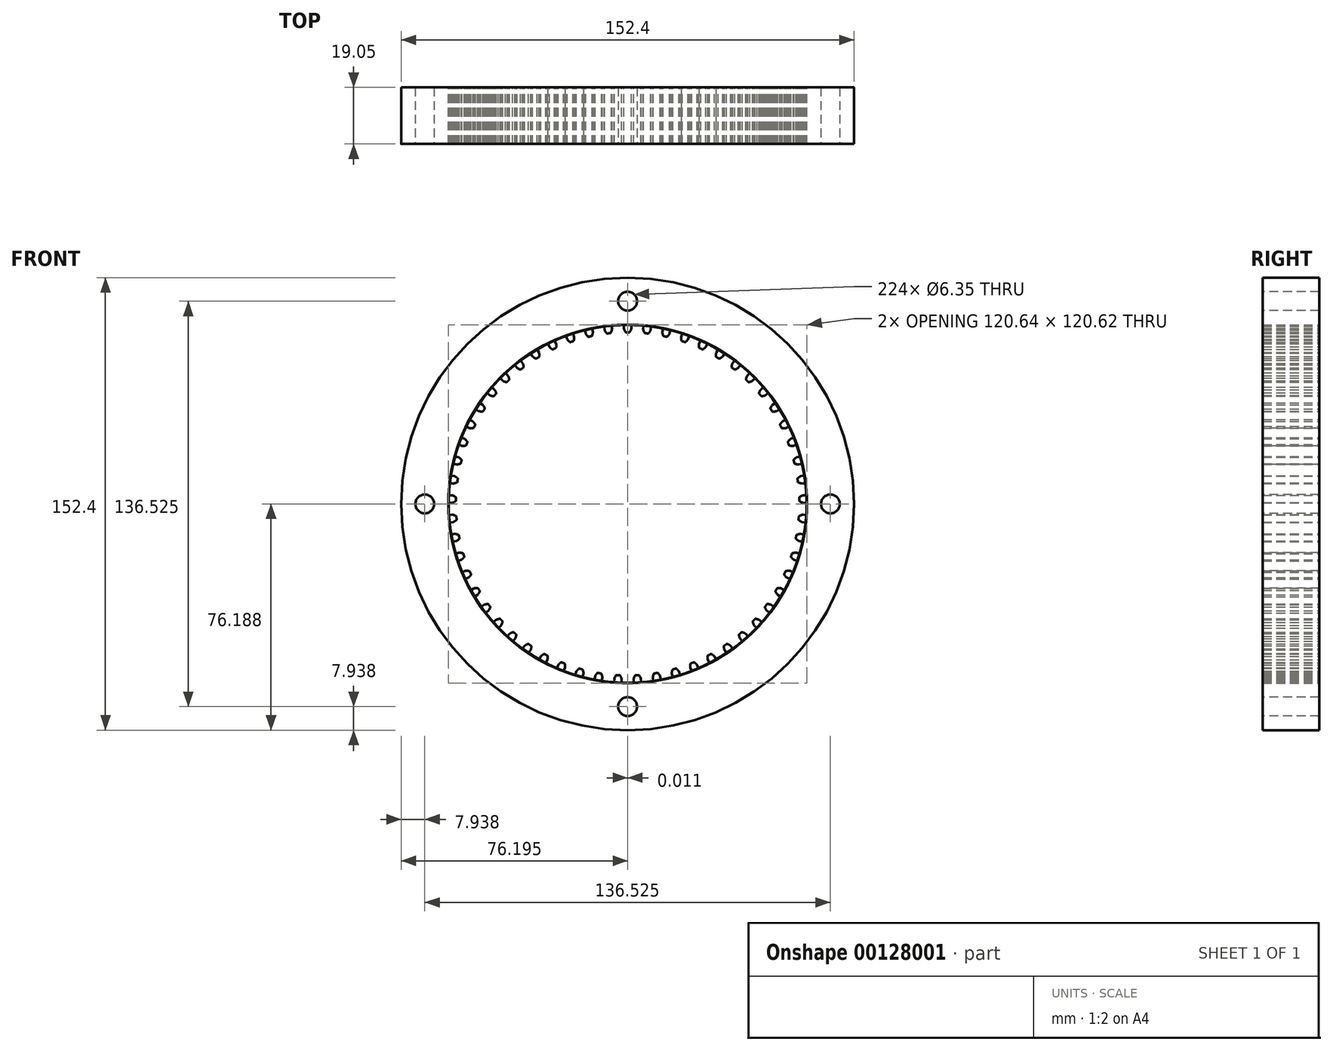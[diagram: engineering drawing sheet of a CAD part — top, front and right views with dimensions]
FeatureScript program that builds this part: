
annotation { "Feature Type Name" : "Feature", "Feature Type Description" : "" }
export const myFeature = defineFeature(function(context is Context, id is Id, definition is map)
    precondition{}
    {
        {
            var Q0;
            Q0=qCreatedBy(makeId("Front.planeOp"),FACE);
            var sketch = newSketch(context, id + "F0", { "sketchPlane" : qUnion([Q0])});
            skCircle(sketch, "E0", {"center": v(0, 0) * mm, "radius": 59.06 * mm, "construction": true});
            skCircle(sketch, "E1", {"center": v(0, 0) * mm, "radius": 60.33 * mm});
            skArc(sketch, "E2", {"start": v(0, 60.33) * mm, "mid": v(0.62, 60.32) * mm, "end": v(1.25, 60.31) * mm});
            skLineSegment(sketch, "E3", {"start": v(1.25, 60.31) * mm, "end": v(1.25, 59.04) * mm});
            skCircle(sketch, "E4", {"center": v(0, 0) * mm, "radius": 57.79 * mm, "construction": true});
            skArc(sketch, "E5", {"start": v(0, 57.79) * mm, "mid": v(0.25, 57.78) * mm, "end": v(0.5, 57.78) * mm});
            skFitSpline(sketch, "E6", {"points": [v(0.63, 57.78) * mm, v(1.25, 59.04) * mm, v(1.25, 60.31) * mm], "startDerivative": vector(1.5, 2.42) * mm, "endDerivative": vector(-0.3, 2.64) * mm});
            skArc(sketch, "E7.filletArc", {"start": v(0.5, 57.78) * mm, "mid": v(0.62, 57.81) * mm, "end": v(0.71, 57.9) * mm});
            skArc(sketch, "E8.MirrorCS", {"start": v(0, 57.79) * mm, "mid": v(-0.25, 57.78) * mm, "end": v(-0.5, 57.78) * mm});
            skArc(sketch, "E9.MirrorCS", {"start": v(-0.5, 57.78) * mm, "mid": v(-0.62, 57.81) * mm, "end": v(-0.71, 57.9) * mm});
            skFitSpline(sketch, "E10.MirrorCS", {"points": [v(-0.63, 57.78) * mm, v(-1.25, 59.04) * mm, v(-1.25, 60.31) * mm], "startDerivative": vector(-1.5, 2.42) * mm, "endDerivative": vector(0.3, 2.64) * mm});
            skLineSegment(sketch, "E11.MirrorCS", {"start": v(-1.25, 60.31) * mm, "end": v(-1.25, 59.04) * mm});
            skCircle(sketch, "E12", {"center": v(0, 0) * mm, "radius": 76.2 * mm});
            skSolve(sketch);
        }
        {
            var Q0;
            Q0=makeQuery(id+"F0.imprint","IMPRINT",FACE,{"disambiguationData":[TD([[makeQuery(id+"F0.imprint","IMPRINT",EDGE,{"derivedFrom":sQuery(id+"F0.wireOp",EDGE,"E12")}),1.0]])]});
            var Q1;
            {var subQ0=sQuery(id+"F0.wireOp",EDGE,"E3");Q1=makeQuery(id+"F0.imprint","IMPRINT",FACE,{"disambiguationData":[TD([[makeQuery(id+"F0.imprint","IMPRINT",EDGE,{"derivedFrom":subQ0}),-1.0]])]});}
            extrude(context, id + "F1", {"entities" : qUnion([Q0, Q1]), "depth" : 19.05 * mm});
        }
        {
            var Q0;
            Q0=makeQuery(id+"F1.opExtrude","SWEPT_BODY",BODY,{"disambiguationData":[OSD([sQuery(id+"F0.wireOp",EDGE,"E1"),sQuery(id+"F0.wireOp",EDGE,"E3"),sQuery(id+"F0.wireOp",EDGE,"E5"),sQuery(id+"F0.wireOp",EDGE,"E6"),sQuery(id+"F0.wireOp",EDGE,"E7.filletArc"),sQuery(id+"F0.wireOp",EDGE,"E8.MirrorCS"),sQuery(id+"F0.wireOp",EDGE,"E9.MirrorCS"),sQuery(id+"F0.wireOp",EDGE,"E10.MirrorCS"),sQuery(id+"F0.wireOp",EDGE,"E11.MirrorCS"),sQuery(id+"F0.wireOp",EDGE,"E12")])]});
            var Q1;
            Q1=makeQuery(id+"F1.opExtrude","SWEPT_FACE",FACE,{"disambiguationData":[OSD([sQuery(id+"F0.wireOp",EDGE,"E1")])]});
            circularPattern(context, id + "F2", {"entities" : qUnion([Q0]), "axis" : qUnion([Q1]), "angle" : 6.32 * degree, "instanceCount" : 57});
        }
        {
            var Q0;
            Q0=makeQuery(id+"F2.opPattern","COPY",FACE,{"derivedFrom":makeQuery(id+"F1.opExtrude","CAP_FACE",FACE,{"disambiguationData":[OSD([sQuery(id+"F0.wireOp",EDGE,"E1"),sQuery(id+"F0.wireOp",EDGE,"E3"),sQuery(id+"F0.wireOp",EDGE,"E5"),sQuery(id+"F0.wireOp",EDGE,"E6"),sQuery(id+"F0.wireOp",EDGE,"E7.filletArc"),sQuery(id+"F0.wireOp",EDGE,"E8.MirrorCS"),sQuery(id+"F0.wireOp",EDGE,"E9.MirrorCS"),sQuery(id+"F0.wireOp",EDGE,"E10.MirrorCS"),sQuery(id+"F0.wireOp",EDGE,"E11.MirrorCS"),sQuery(id+"F0.wireOp",EDGE,"E12")])],"isStart":false}),"instanceName":"27"});
            var sketch = newSketch(context, id + "F3", { "sketchPlane" : qUnion([Q0])});
            skCircle(sketch, "E13", {"center": v(0, 68.26) * mm, "radius": 3.18 * mm});
            skCircle(sketch, "E14.1.0", {"center": v(-68.26, 0) * mm, "radius": 3.18 * mm});
            skCircle(sketch, "E14.2.0", {"center": v(0, -68.26) * mm, "radius": 3.18 * mm});
            skCircle(sketch, "E14.3.0", {"center": v(68.26, 0) * mm, "radius": 3.18 * mm});
            skPoint(sketch, "E14.center", {"position": v(0, 0) * mm});
            skSolve(sketch);
        }
        {
            var Q0;
            Q0=sQuery(id+"F3.wireOp",VERTEX,"E13.center");
            var Q1;
            Q1=sQuery(id+"F3.wireOp",VERTEX,"E14.3.0.center");
            var Q2;
            Q2=sQuery(id+"F3.wireOp",VERTEX,"E14.2.0.center");
            var Q3;
            Q3=sQuery(id+"F3.wireOp",VERTEX,"E14.1.0.center");
            var Q4;
            Q4=makeQuery(id+"F1.opExtrude","SWEPT_BODY",BODY,{"disambiguationData":[OSD([sQuery(id+"F0.wireOp",EDGE,"E1"),sQuery(id+"F0.wireOp",EDGE,"E3"),sQuery(id+"F0.wireOp",EDGE,"E5"),sQuery(id+"F0.wireOp",EDGE,"E6"),sQuery(id+"F0.wireOp",EDGE,"E7.filletArc"),sQuery(id+"F0.wireOp",EDGE,"E8.MirrorCS"),sQuery(id+"F0.wireOp",EDGE,"E9.MirrorCS"),sQuery(id+"F0.wireOp",EDGE,"E10.MirrorCS"),sQuery(id+"F0.wireOp",EDGE,"E11.MirrorCS"),sQuery(id+"F0.wireOp",EDGE,"E12")])]});
            var Q5;
            Q5=makeQuery(id+"F2.opPattern","COPY",BODY,{"derivedFrom":makeQuery(id+"F1.opExtrude","SWEPT_BODY",BODY,{"disambiguationData":[OSD([sQuery(id+"F0.wireOp",EDGE,"E1"),sQuery(id+"F0.wireOp",EDGE,"E3"),sQuery(id+"F0.wireOp",EDGE,"E5"),sQuery(id+"F0.wireOp",EDGE,"E6"),sQuery(id+"F0.wireOp",EDGE,"E7.filletArc"),sQuery(id+"F0.wireOp",EDGE,"E8.MirrorCS"),sQuery(id+"F0.wireOp",EDGE,"E9.MirrorCS"),sQuery(id+"F0.wireOp",EDGE,"E10.MirrorCS"),sQuery(id+"F0.wireOp",EDGE,"E11.MirrorCS"),sQuery(id+"F0.wireOp",EDGE,"E12")])]}),"instanceName":"1"});
            var Q6;
            Q6=makeQuery(id+"F2.opPattern","COPY",BODY,{"derivedFrom":makeQuery(id+"F1.opExtrude","SWEPT_BODY",BODY,{"disambiguationData":[OSD([sQuery(id+"F0.wireOp",EDGE,"E1"),sQuery(id+"F0.wireOp",EDGE,"E3"),sQuery(id+"F0.wireOp",EDGE,"E5"),sQuery(id+"F0.wireOp",EDGE,"E6"),sQuery(id+"F0.wireOp",EDGE,"E7.filletArc"),sQuery(id+"F0.wireOp",EDGE,"E8.MirrorCS"),sQuery(id+"F0.wireOp",EDGE,"E9.MirrorCS"),sQuery(id+"F0.wireOp",EDGE,"E10.MirrorCS"),sQuery(id+"F0.wireOp",EDGE,"E11.MirrorCS"),sQuery(id+"F0.wireOp",EDGE,"E12")])]}),"instanceName":"2"});
            var Q7;
            Q7=makeQuery(id+"F2.opPattern","COPY",BODY,{"derivedFrom":makeQuery(id+"F1.opExtrude","SWEPT_BODY",BODY,{"disambiguationData":[OSD([sQuery(id+"F0.wireOp",EDGE,"E1"),sQuery(id+"F0.wireOp",EDGE,"E3"),sQuery(id+"F0.wireOp",EDGE,"E5"),sQuery(id+"F0.wireOp",EDGE,"E6"),sQuery(id+"F0.wireOp",EDGE,"E7.filletArc"),sQuery(id+"F0.wireOp",EDGE,"E8.MirrorCS"),sQuery(id+"F0.wireOp",EDGE,"E9.MirrorCS"),sQuery(id+"F0.wireOp",EDGE,"E10.MirrorCS"),sQuery(id+"F0.wireOp",EDGE,"E11.MirrorCS"),sQuery(id+"F0.wireOp",EDGE,"E12")])]}),"instanceName":"3"});
            var Q8;
            Q8=makeQuery(id+"F2.opPattern","COPY",BODY,{"derivedFrom":makeQuery(id+"F1.opExtrude","SWEPT_BODY",BODY,{"disambiguationData":[OSD([sQuery(id+"F0.wireOp",EDGE,"E1"),sQuery(id+"F0.wireOp",EDGE,"E3"),sQuery(id+"F0.wireOp",EDGE,"E5"),sQuery(id+"F0.wireOp",EDGE,"E6"),sQuery(id+"F0.wireOp",EDGE,"E7.filletArc"),sQuery(id+"F0.wireOp",EDGE,"E8.MirrorCS"),sQuery(id+"F0.wireOp",EDGE,"E9.MirrorCS"),sQuery(id+"F0.wireOp",EDGE,"E10.MirrorCS"),sQuery(id+"F0.wireOp",EDGE,"E11.MirrorCS"),sQuery(id+"F0.wireOp",EDGE,"E12")])]}),"instanceName":"4"});
            var Q9;
            Q9=makeQuery(id+"F2.opPattern","COPY",BODY,{"derivedFrom":makeQuery(id+"F1.opExtrude","SWEPT_BODY",BODY,{"disambiguationData":[OSD([sQuery(id+"F0.wireOp",EDGE,"E1"),sQuery(id+"F0.wireOp",EDGE,"E3"),sQuery(id+"F0.wireOp",EDGE,"E5"),sQuery(id+"F0.wireOp",EDGE,"E6"),sQuery(id+"F0.wireOp",EDGE,"E7.filletArc"),sQuery(id+"F0.wireOp",EDGE,"E8.MirrorCS"),sQuery(id+"F0.wireOp",EDGE,"E9.MirrorCS"),sQuery(id+"F0.wireOp",EDGE,"E10.MirrorCS"),sQuery(id+"F0.wireOp",EDGE,"E11.MirrorCS"),sQuery(id+"F0.wireOp",EDGE,"E12")])]}),"instanceName":"5"});
            var Q10;
            Q10=makeQuery(id+"F2.opPattern","COPY",BODY,{"derivedFrom":makeQuery(id+"F1.opExtrude","SWEPT_BODY",BODY,{"disambiguationData":[OSD([sQuery(id+"F0.wireOp",EDGE,"E1"),sQuery(id+"F0.wireOp",EDGE,"E3"),sQuery(id+"F0.wireOp",EDGE,"E5"),sQuery(id+"F0.wireOp",EDGE,"E6"),sQuery(id+"F0.wireOp",EDGE,"E7.filletArc"),sQuery(id+"F0.wireOp",EDGE,"E8.MirrorCS"),sQuery(id+"F0.wireOp",EDGE,"E9.MirrorCS"),sQuery(id+"F0.wireOp",EDGE,"E10.MirrorCS"),sQuery(id+"F0.wireOp",EDGE,"E11.MirrorCS"),sQuery(id+"F0.wireOp",EDGE,"E12")])]}),"instanceName":"6"});
            var Q11;
            Q11=makeQuery(id+"F2.opPattern","COPY",BODY,{"derivedFrom":makeQuery(id+"F1.opExtrude","SWEPT_BODY",BODY,{"disambiguationData":[OSD([sQuery(id+"F0.wireOp",EDGE,"E1"),sQuery(id+"F0.wireOp",EDGE,"E3"),sQuery(id+"F0.wireOp",EDGE,"E5"),sQuery(id+"F0.wireOp",EDGE,"E6"),sQuery(id+"F0.wireOp",EDGE,"E7.filletArc"),sQuery(id+"F0.wireOp",EDGE,"E8.MirrorCS"),sQuery(id+"F0.wireOp",EDGE,"E9.MirrorCS"),sQuery(id+"F0.wireOp",EDGE,"E10.MirrorCS"),sQuery(id+"F0.wireOp",EDGE,"E11.MirrorCS"),sQuery(id+"F0.wireOp",EDGE,"E12")])]}),"instanceName":"7"});
            var Q12;
            Q12=makeQuery(id+"F2.opPattern","COPY",BODY,{"derivedFrom":makeQuery(id+"F1.opExtrude","SWEPT_BODY",BODY,{"disambiguationData":[OSD([sQuery(id+"F0.wireOp",EDGE,"E1"),sQuery(id+"F0.wireOp",EDGE,"E3"),sQuery(id+"F0.wireOp",EDGE,"E5"),sQuery(id+"F0.wireOp",EDGE,"E6"),sQuery(id+"F0.wireOp",EDGE,"E7.filletArc"),sQuery(id+"F0.wireOp",EDGE,"E8.MirrorCS"),sQuery(id+"F0.wireOp",EDGE,"E9.MirrorCS"),sQuery(id+"F0.wireOp",EDGE,"E10.MirrorCS"),sQuery(id+"F0.wireOp",EDGE,"E11.MirrorCS"),sQuery(id+"F0.wireOp",EDGE,"E12")])]}),"instanceName":"8"});
            var Q13;
            Q13=makeQuery(id+"F2.opPattern","COPY",BODY,{"derivedFrom":makeQuery(id+"F1.opExtrude","SWEPT_BODY",BODY,{"disambiguationData":[OSD([sQuery(id+"F0.wireOp",EDGE,"E1"),sQuery(id+"F0.wireOp",EDGE,"E3"),sQuery(id+"F0.wireOp",EDGE,"E5"),sQuery(id+"F0.wireOp",EDGE,"E6"),sQuery(id+"F0.wireOp",EDGE,"E7.filletArc"),sQuery(id+"F0.wireOp",EDGE,"E8.MirrorCS"),sQuery(id+"F0.wireOp",EDGE,"E9.MirrorCS"),sQuery(id+"F0.wireOp",EDGE,"E10.MirrorCS"),sQuery(id+"F0.wireOp",EDGE,"E11.MirrorCS"),sQuery(id+"F0.wireOp",EDGE,"E12")])]}),"instanceName":"9"});
            var Q14;
            Q14=makeQuery(id+"F2.opPattern","COPY",BODY,{"derivedFrom":makeQuery(id+"F1.opExtrude","SWEPT_BODY",BODY,{"disambiguationData":[OSD([sQuery(id+"F0.wireOp",EDGE,"E1"),sQuery(id+"F0.wireOp",EDGE,"E3"),sQuery(id+"F0.wireOp",EDGE,"E5"),sQuery(id+"F0.wireOp",EDGE,"E6"),sQuery(id+"F0.wireOp",EDGE,"E7.filletArc"),sQuery(id+"F0.wireOp",EDGE,"E8.MirrorCS"),sQuery(id+"F0.wireOp",EDGE,"E9.MirrorCS"),sQuery(id+"F0.wireOp",EDGE,"E10.MirrorCS"),sQuery(id+"F0.wireOp",EDGE,"E11.MirrorCS"),sQuery(id+"F0.wireOp",EDGE,"E12")])]}),"instanceName":"10"});
            var Q15;
            Q15=makeQuery(id+"F2.opPattern","COPY",BODY,{"derivedFrom":makeQuery(id+"F1.opExtrude","SWEPT_BODY",BODY,{"disambiguationData":[OSD([sQuery(id+"F0.wireOp",EDGE,"E1"),sQuery(id+"F0.wireOp",EDGE,"E3"),sQuery(id+"F0.wireOp",EDGE,"E5"),sQuery(id+"F0.wireOp",EDGE,"E6"),sQuery(id+"F0.wireOp",EDGE,"E7.filletArc"),sQuery(id+"F0.wireOp",EDGE,"E8.MirrorCS"),sQuery(id+"F0.wireOp",EDGE,"E9.MirrorCS"),sQuery(id+"F0.wireOp",EDGE,"E10.MirrorCS"),sQuery(id+"F0.wireOp",EDGE,"E11.MirrorCS"),sQuery(id+"F0.wireOp",EDGE,"E12")])]}),"instanceName":"11"});
            var Q16;
            Q16=makeQuery(id+"F2.opPattern","COPY",BODY,{"derivedFrom":makeQuery(id+"F1.opExtrude","SWEPT_BODY",BODY,{"disambiguationData":[OSD([sQuery(id+"F0.wireOp",EDGE,"E1"),sQuery(id+"F0.wireOp",EDGE,"E3"),sQuery(id+"F0.wireOp",EDGE,"E5"),sQuery(id+"F0.wireOp",EDGE,"E6"),sQuery(id+"F0.wireOp",EDGE,"E7.filletArc"),sQuery(id+"F0.wireOp",EDGE,"E8.MirrorCS"),sQuery(id+"F0.wireOp",EDGE,"E9.MirrorCS"),sQuery(id+"F0.wireOp",EDGE,"E10.MirrorCS"),sQuery(id+"F0.wireOp",EDGE,"E11.MirrorCS"),sQuery(id+"F0.wireOp",EDGE,"E12")])]}),"instanceName":"12"});
            var Q17;
            Q17=makeQuery(id+"F2.opPattern","COPY",BODY,{"derivedFrom":makeQuery(id+"F1.opExtrude","SWEPT_BODY",BODY,{"disambiguationData":[OSD([sQuery(id+"F0.wireOp",EDGE,"E1"),sQuery(id+"F0.wireOp",EDGE,"E3"),sQuery(id+"F0.wireOp",EDGE,"E5"),sQuery(id+"F0.wireOp",EDGE,"E6"),sQuery(id+"F0.wireOp",EDGE,"E7.filletArc"),sQuery(id+"F0.wireOp",EDGE,"E8.MirrorCS"),sQuery(id+"F0.wireOp",EDGE,"E9.MirrorCS"),sQuery(id+"F0.wireOp",EDGE,"E10.MirrorCS"),sQuery(id+"F0.wireOp",EDGE,"E11.MirrorCS"),sQuery(id+"F0.wireOp",EDGE,"E12")])]}),"instanceName":"13"});
            var Q18;
            Q18=makeQuery(id+"F2.opPattern","COPY",BODY,{"derivedFrom":makeQuery(id+"F1.opExtrude","SWEPT_BODY",BODY,{"disambiguationData":[OSD([sQuery(id+"F0.wireOp",EDGE,"E1"),sQuery(id+"F0.wireOp",EDGE,"E3"),sQuery(id+"F0.wireOp",EDGE,"E5"),sQuery(id+"F0.wireOp",EDGE,"E6"),sQuery(id+"F0.wireOp",EDGE,"E7.filletArc"),sQuery(id+"F0.wireOp",EDGE,"E8.MirrorCS"),sQuery(id+"F0.wireOp",EDGE,"E9.MirrorCS"),sQuery(id+"F0.wireOp",EDGE,"E10.MirrorCS"),sQuery(id+"F0.wireOp",EDGE,"E11.MirrorCS"),sQuery(id+"F0.wireOp",EDGE,"E12")])]}),"instanceName":"14"});
            var Q19;
            Q19=makeQuery(id+"F2.opPattern","COPY",BODY,{"derivedFrom":makeQuery(id+"F1.opExtrude","SWEPT_BODY",BODY,{"disambiguationData":[OSD([sQuery(id+"F0.wireOp",EDGE,"E1"),sQuery(id+"F0.wireOp",EDGE,"E3"),sQuery(id+"F0.wireOp",EDGE,"E5"),sQuery(id+"F0.wireOp",EDGE,"E6"),sQuery(id+"F0.wireOp",EDGE,"E7.filletArc"),sQuery(id+"F0.wireOp",EDGE,"E8.MirrorCS"),sQuery(id+"F0.wireOp",EDGE,"E9.MirrorCS"),sQuery(id+"F0.wireOp",EDGE,"E10.MirrorCS"),sQuery(id+"F0.wireOp",EDGE,"E11.MirrorCS"),sQuery(id+"F0.wireOp",EDGE,"E12")])]}),"instanceName":"15"});
            var Q20;
            Q20=makeQuery(id+"F2.opPattern","COPY",BODY,{"derivedFrom":makeQuery(id+"F1.opExtrude","SWEPT_BODY",BODY,{"disambiguationData":[OSD([sQuery(id+"F0.wireOp",EDGE,"E1"),sQuery(id+"F0.wireOp",EDGE,"E3"),sQuery(id+"F0.wireOp",EDGE,"E5"),sQuery(id+"F0.wireOp",EDGE,"E6"),sQuery(id+"F0.wireOp",EDGE,"E7.filletArc"),sQuery(id+"F0.wireOp",EDGE,"E8.MirrorCS"),sQuery(id+"F0.wireOp",EDGE,"E9.MirrorCS"),sQuery(id+"F0.wireOp",EDGE,"E10.MirrorCS"),sQuery(id+"F0.wireOp",EDGE,"E11.MirrorCS"),sQuery(id+"F0.wireOp",EDGE,"E12")])]}),"instanceName":"16"});
            var Q21;
            Q21=makeQuery(id+"F2.opPattern","COPY",BODY,{"derivedFrom":makeQuery(id+"F1.opExtrude","SWEPT_BODY",BODY,{"disambiguationData":[OSD([sQuery(id+"F0.wireOp",EDGE,"E1"),sQuery(id+"F0.wireOp",EDGE,"E3"),sQuery(id+"F0.wireOp",EDGE,"E5"),sQuery(id+"F0.wireOp",EDGE,"E6"),sQuery(id+"F0.wireOp",EDGE,"E7.filletArc"),sQuery(id+"F0.wireOp",EDGE,"E8.MirrorCS"),sQuery(id+"F0.wireOp",EDGE,"E9.MirrorCS"),sQuery(id+"F0.wireOp",EDGE,"E10.MirrorCS"),sQuery(id+"F0.wireOp",EDGE,"E11.MirrorCS"),sQuery(id+"F0.wireOp",EDGE,"E12")])]}),"instanceName":"17"});
            var Q22;
            Q22=makeQuery(id+"F2.opPattern","COPY",BODY,{"derivedFrom":makeQuery(id+"F1.opExtrude","SWEPT_BODY",BODY,{"disambiguationData":[OSD([sQuery(id+"F0.wireOp",EDGE,"E1"),sQuery(id+"F0.wireOp",EDGE,"E3"),sQuery(id+"F0.wireOp",EDGE,"E5"),sQuery(id+"F0.wireOp",EDGE,"E6"),sQuery(id+"F0.wireOp",EDGE,"E7.filletArc"),sQuery(id+"F0.wireOp",EDGE,"E8.MirrorCS"),sQuery(id+"F0.wireOp",EDGE,"E9.MirrorCS"),sQuery(id+"F0.wireOp",EDGE,"E10.MirrorCS"),sQuery(id+"F0.wireOp",EDGE,"E11.MirrorCS"),sQuery(id+"F0.wireOp",EDGE,"E12")])]}),"instanceName":"18"});
            var Q23;
            Q23=makeQuery(id+"F2.opPattern","COPY",BODY,{"derivedFrom":makeQuery(id+"F1.opExtrude","SWEPT_BODY",BODY,{"disambiguationData":[OSD([sQuery(id+"F0.wireOp",EDGE,"E1"),sQuery(id+"F0.wireOp",EDGE,"E3"),sQuery(id+"F0.wireOp",EDGE,"E5"),sQuery(id+"F0.wireOp",EDGE,"E6"),sQuery(id+"F0.wireOp",EDGE,"E7.filletArc"),sQuery(id+"F0.wireOp",EDGE,"E8.MirrorCS"),sQuery(id+"F0.wireOp",EDGE,"E9.MirrorCS"),sQuery(id+"F0.wireOp",EDGE,"E10.MirrorCS"),sQuery(id+"F0.wireOp",EDGE,"E11.MirrorCS"),sQuery(id+"F0.wireOp",EDGE,"E12")])]}),"instanceName":"19"});
            var Q24;
            Q24=makeQuery(id+"F2.opPattern","COPY",BODY,{"derivedFrom":makeQuery(id+"F1.opExtrude","SWEPT_BODY",BODY,{"disambiguationData":[OSD([sQuery(id+"F0.wireOp",EDGE,"E1"),sQuery(id+"F0.wireOp",EDGE,"E3"),sQuery(id+"F0.wireOp",EDGE,"E5"),sQuery(id+"F0.wireOp",EDGE,"E6"),sQuery(id+"F0.wireOp",EDGE,"E7.filletArc"),sQuery(id+"F0.wireOp",EDGE,"E8.MirrorCS"),sQuery(id+"F0.wireOp",EDGE,"E9.MirrorCS"),sQuery(id+"F0.wireOp",EDGE,"E10.MirrorCS"),sQuery(id+"F0.wireOp",EDGE,"E11.MirrorCS"),sQuery(id+"F0.wireOp",EDGE,"E12")])]}),"instanceName":"20"});
            var Q25;
            Q25=makeQuery(id+"F2.opPattern","COPY",BODY,{"derivedFrom":makeQuery(id+"F1.opExtrude","SWEPT_BODY",BODY,{"disambiguationData":[OSD([sQuery(id+"F0.wireOp",EDGE,"E1"),sQuery(id+"F0.wireOp",EDGE,"E3"),sQuery(id+"F0.wireOp",EDGE,"E5"),sQuery(id+"F0.wireOp",EDGE,"E6"),sQuery(id+"F0.wireOp",EDGE,"E7.filletArc"),sQuery(id+"F0.wireOp",EDGE,"E8.MirrorCS"),sQuery(id+"F0.wireOp",EDGE,"E9.MirrorCS"),sQuery(id+"F0.wireOp",EDGE,"E10.MirrorCS"),sQuery(id+"F0.wireOp",EDGE,"E11.MirrorCS"),sQuery(id+"F0.wireOp",EDGE,"E12")])]}),"instanceName":"21"});
            var Q26;
            Q26=makeQuery(id+"F2.opPattern","COPY",BODY,{"derivedFrom":makeQuery(id+"F1.opExtrude","SWEPT_BODY",BODY,{"disambiguationData":[OSD([sQuery(id+"F0.wireOp",EDGE,"E1"),sQuery(id+"F0.wireOp",EDGE,"E3"),sQuery(id+"F0.wireOp",EDGE,"E5"),sQuery(id+"F0.wireOp",EDGE,"E6"),sQuery(id+"F0.wireOp",EDGE,"E7.filletArc"),sQuery(id+"F0.wireOp",EDGE,"E8.MirrorCS"),sQuery(id+"F0.wireOp",EDGE,"E9.MirrorCS"),sQuery(id+"F0.wireOp",EDGE,"E10.MirrorCS"),sQuery(id+"F0.wireOp",EDGE,"E11.MirrorCS"),sQuery(id+"F0.wireOp",EDGE,"E12")])]}),"instanceName":"22"});
            var Q27;
            Q27=makeQuery(id+"F2.opPattern","COPY",BODY,{"derivedFrom":makeQuery(id+"F1.opExtrude","SWEPT_BODY",BODY,{"disambiguationData":[OSD([sQuery(id+"F0.wireOp",EDGE,"E1"),sQuery(id+"F0.wireOp",EDGE,"E3"),sQuery(id+"F0.wireOp",EDGE,"E5"),sQuery(id+"F0.wireOp",EDGE,"E6"),sQuery(id+"F0.wireOp",EDGE,"E7.filletArc"),sQuery(id+"F0.wireOp",EDGE,"E8.MirrorCS"),sQuery(id+"F0.wireOp",EDGE,"E9.MirrorCS"),sQuery(id+"F0.wireOp",EDGE,"E10.MirrorCS"),sQuery(id+"F0.wireOp",EDGE,"E11.MirrorCS"),sQuery(id+"F0.wireOp",EDGE,"E12")])]}),"instanceName":"23"});
            var Q28;
            Q28=makeQuery(id+"F2.opPattern","COPY",BODY,{"derivedFrom":makeQuery(id+"F1.opExtrude","SWEPT_BODY",BODY,{"disambiguationData":[OSD([sQuery(id+"F0.wireOp",EDGE,"E1"),sQuery(id+"F0.wireOp",EDGE,"E3"),sQuery(id+"F0.wireOp",EDGE,"E5"),sQuery(id+"F0.wireOp",EDGE,"E6"),sQuery(id+"F0.wireOp",EDGE,"E7.filletArc"),sQuery(id+"F0.wireOp",EDGE,"E8.MirrorCS"),sQuery(id+"F0.wireOp",EDGE,"E9.MirrorCS"),sQuery(id+"F0.wireOp",EDGE,"E10.MirrorCS"),sQuery(id+"F0.wireOp",EDGE,"E11.MirrorCS"),sQuery(id+"F0.wireOp",EDGE,"E12")])]}),"instanceName":"24"});
            var Q29;
            Q29=makeQuery(id+"F2.opPattern","COPY",BODY,{"derivedFrom":makeQuery(id+"F1.opExtrude","SWEPT_BODY",BODY,{"disambiguationData":[OSD([sQuery(id+"F0.wireOp",EDGE,"E1"),sQuery(id+"F0.wireOp",EDGE,"E3"),sQuery(id+"F0.wireOp",EDGE,"E5"),sQuery(id+"F0.wireOp",EDGE,"E6"),sQuery(id+"F0.wireOp",EDGE,"E7.filletArc"),sQuery(id+"F0.wireOp",EDGE,"E8.MirrorCS"),sQuery(id+"F0.wireOp",EDGE,"E9.MirrorCS"),sQuery(id+"F0.wireOp",EDGE,"E10.MirrorCS"),sQuery(id+"F0.wireOp",EDGE,"E11.MirrorCS"),sQuery(id+"F0.wireOp",EDGE,"E12")])]}),"instanceName":"25"});
            var Q30;
            Q30=makeQuery(id+"F2.opPattern","COPY",BODY,{"derivedFrom":makeQuery(id+"F1.opExtrude","SWEPT_BODY",BODY,{"disambiguationData":[OSD([sQuery(id+"F0.wireOp",EDGE,"E1"),sQuery(id+"F0.wireOp",EDGE,"E3"),sQuery(id+"F0.wireOp",EDGE,"E5"),sQuery(id+"F0.wireOp",EDGE,"E6"),sQuery(id+"F0.wireOp",EDGE,"E7.filletArc"),sQuery(id+"F0.wireOp",EDGE,"E8.MirrorCS"),sQuery(id+"F0.wireOp",EDGE,"E9.MirrorCS"),sQuery(id+"F0.wireOp",EDGE,"E10.MirrorCS"),sQuery(id+"F0.wireOp",EDGE,"E11.MirrorCS"),sQuery(id+"F0.wireOp",EDGE,"E12")])]}),"instanceName":"26"});
            var Q31;
            Q31=makeQuery(id+"F2.opPattern","COPY",BODY,{"derivedFrom":makeQuery(id+"F1.opExtrude","SWEPT_BODY",BODY,{"disambiguationData":[OSD([sQuery(id+"F0.wireOp",EDGE,"E1"),sQuery(id+"F0.wireOp",EDGE,"E3"),sQuery(id+"F0.wireOp",EDGE,"E5"),sQuery(id+"F0.wireOp",EDGE,"E6"),sQuery(id+"F0.wireOp",EDGE,"E7.filletArc"),sQuery(id+"F0.wireOp",EDGE,"E8.MirrorCS"),sQuery(id+"F0.wireOp",EDGE,"E9.MirrorCS"),sQuery(id+"F0.wireOp",EDGE,"E10.MirrorCS"),sQuery(id+"F0.wireOp",EDGE,"E11.MirrorCS"),sQuery(id+"F0.wireOp",EDGE,"E12")])]}),"instanceName":"27"});
            var Q32;
            Q32=makeQuery(id+"F2.opPattern","COPY",BODY,{"derivedFrom":makeQuery(id+"F1.opExtrude","SWEPT_BODY",BODY,{"disambiguationData":[OSD([sQuery(id+"F0.wireOp",EDGE,"E1"),sQuery(id+"F0.wireOp",EDGE,"E3"),sQuery(id+"F0.wireOp",EDGE,"E5"),sQuery(id+"F0.wireOp",EDGE,"E6"),sQuery(id+"F0.wireOp",EDGE,"E7.filletArc"),sQuery(id+"F0.wireOp",EDGE,"E8.MirrorCS"),sQuery(id+"F0.wireOp",EDGE,"E9.MirrorCS"),sQuery(id+"F0.wireOp",EDGE,"E10.MirrorCS"),sQuery(id+"F0.wireOp",EDGE,"E11.MirrorCS"),sQuery(id+"F0.wireOp",EDGE,"E12")])]}),"instanceName":"28"});
            var Q33;
            Q33=makeQuery(id+"F2.opPattern","COPY",BODY,{"derivedFrom":makeQuery(id+"F1.opExtrude","SWEPT_BODY",BODY,{"disambiguationData":[OSD([sQuery(id+"F0.wireOp",EDGE,"E1"),sQuery(id+"F0.wireOp",EDGE,"E3"),sQuery(id+"F0.wireOp",EDGE,"E5"),sQuery(id+"F0.wireOp",EDGE,"E6"),sQuery(id+"F0.wireOp",EDGE,"E7.filletArc"),sQuery(id+"F0.wireOp",EDGE,"E8.MirrorCS"),sQuery(id+"F0.wireOp",EDGE,"E9.MirrorCS"),sQuery(id+"F0.wireOp",EDGE,"E10.MirrorCS"),sQuery(id+"F0.wireOp",EDGE,"E11.MirrorCS"),sQuery(id+"F0.wireOp",EDGE,"E12")])]}),"instanceName":"29"});
            var Q34;
            Q34=makeQuery(id+"F2.opPattern","COPY",BODY,{"derivedFrom":makeQuery(id+"F1.opExtrude","SWEPT_BODY",BODY,{"disambiguationData":[OSD([sQuery(id+"F0.wireOp",EDGE,"E1"),sQuery(id+"F0.wireOp",EDGE,"E3"),sQuery(id+"F0.wireOp",EDGE,"E5"),sQuery(id+"F0.wireOp",EDGE,"E6"),sQuery(id+"F0.wireOp",EDGE,"E7.filletArc"),sQuery(id+"F0.wireOp",EDGE,"E8.MirrorCS"),sQuery(id+"F0.wireOp",EDGE,"E9.MirrorCS"),sQuery(id+"F0.wireOp",EDGE,"E10.MirrorCS"),sQuery(id+"F0.wireOp",EDGE,"E11.MirrorCS"),sQuery(id+"F0.wireOp",EDGE,"E12")])]}),"instanceName":"30"});
            var Q35;
            Q35=makeQuery(id+"F2.opPattern","COPY",BODY,{"derivedFrom":makeQuery(id+"F1.opExtrude","SWEPT_BODY",BODY,{"disambiguationData":[OSD([sQuery(id+"F0.wireOp",EDGE,"E1"),sQuery(id+"F0.wireOp",EDGE,"E3"),sQuery(id+"F0.wireOp",EDGE,"E5"),sQuery(id+"F0.wireOp",EDGE,"E6"),sQuery(id+"F0.wireOp",EDGE,"E7.filletArc"),sQuery(id+"F0.wireOp",EDGE,"E8.MirrorCS"),sQuery(id+"F0.wireOp",EDGE,"E9.MirrorCS"),sQuery(id+"F0.wireOp",EDGE,"E10.MirrorCS"),sQuery(id+"F0.wireOp",EDGE,"E11.MirrorCS"),sQuery(id+"F0.wireOp",EDGE,"E12")])]}),"instanceName":"31"});
            var Q36;
            Q36=makeQuery(id+"F2.opPattern","COPY",BODY,{"derivedFrom":makeQuery(id+"F1.opExtrude","SWEPT_BODY",BODY,{"disambiguationData":[OSD([sQuery(id+"F0.wireOp",EDGE,"E1"),sQuery(id+"F0.wireOp",EDGE,"E3"),sQuery(id+"F0.wireOp",EDGE,"E5"),sQuery(id+"F0.wireOp",EDGE,"E6"),sQuery(id+"F0.wireOp",EDGE,"E7.filletArc"),sQuery(id+"F0.wireOp",EDGE,"E8.MirrorCS"),sQuery(id+"F0.wireOp",EDGE,"E9.MirrorCS"),sQuery(id+"F0.wireOp",EDGE,"E10.MirrorCS"),sQuery(id+"F0.wireOp",EDGE,"E11.MirrorCS"),sQuery(id+"F0.wireOp",EDGE,"E12")])]}),"instanceName":"32"});
            var Q37;
            Q37=makeQuery(id+"F2.opPattern","COPY",BODY,{"derivedFrom":makeQuery(id+"F1.opExtrude","SWEPT_BODY",BODY,{"disambiguationData":[OSD([sQuery(id+"F0.wireOp",EDGE,"E1"),sQuery(id+"F0.wireOp",EDGE,"E3"),sQuery(id+"F0.wireOp",EDGE,"E5"),sQuery(id+"F0.wireOp",EDGE,"E6"),sQuery(id+"F0.wireOp",EDGE,"E7.filletArc"),sQuery(id+"F0.wireOp",EDGE,"E8.MirrorCS"),sQuery(id+"F0.wireOp",EDGE,"E9.MirrorCS"),sQuery(id+"F0.wireOp",EDGE,"E10.MirrorCS"),sQuery(id+"F0.wireOp",EDGE,"E11.MirrorCS"),sQuery(id+"F0.wireOp",EDGE,"E12")])]}),"instanceName":"33"});
            var Q38;
            Q38=makeQuery(id+"F2.opPattern","COPY",BODY,{"derivedFrom":makeQuery(id+"F1.opExtrude","SWEPT_BODY",BODY,{"disambiguationData":[OSD([sQuery(id+"F0.wireOp",EDGE,"E1"),sQuery(id+"F0.wireOp",EDGE,"E3"),sQuery(id+"F0.wireOp",EDGE,"E5"),sQuery(id+"F0.wireOp",EDGE,"E6"),sQuery(id+"F0.wireOp",EDGE,"E7.filletArc"),sQuery(id+"F0.wireOp",EDGE,"E8.MirrorCS"),sQuery(id+"F0.wireOp",EDGE,"E9.MirrorCS"),sQuery(id+"F0.wireOp",EDGE,"E10.MirrorCS"),sQuery(id+"F0.wireOp",EDGE,"E11.MirrorCS"),sQuery(id+"F0.wireOp",EDGE,"E12")])]}),"instanceName":"34"});
            var Q39;
            Q39=makeQuery(id+"F2.opPattern","COPY",BODY,{"derivedFrom":makeQuery(id+"F1.opExtrude","SWEPT_BODY",BODY,{"disambiguationData":[OSD([sQuery(id+"F0.wireOp",EDGE,"E1"),sQuery(id+"F0.wireOp",EDGE,"E3"),sQuery(id+"F0.wireOp",EDGE,"E5"),sQuery(id+"F0.wireOp",EDGE,"E6"),sQuery(id+"F0.wireOp",EDGE,"E7.filletArc"),sQuery(id+"F0.wireOp",EDGE,"E8.MirrorCS"),sQuery(id+"F0.wireOp",EDGE,"E9.MirrorCS"),sQuery(id+"F0.wireOp",EDGE,"E10.MirrorCS"),sQuery(id+"F0.wireOp",EDGE,"E11.MirrorCS"),sQuery(id+"F0.wireOp",EDGE,"E12")])]}),"instanceName":"35"});
            var Q40;
            Q40=makeQuery(id+"F2.opPattern","COPY",BODY,{"derivedFrom":makeQuery(id+"F1.opExtrude","SWEPT_BODY",BODY,{"disambiguationData":[OSD([sQuery(id+"F0.wireOp",EDGE,"E1"),sQuery(id+"F0.wireOp",EDGE,"E3"),sQuery(id+"F0.wireOp",EDGE,"E5"),sQuery(id+"F0.wireOp",EDGE,"E6"),sQuery(id+"F0.wireOp",EDGE,"E7.filletArc"),sQuery(id+"F0.wireOp",EDGE,"E8.MirrorCS"),sQuery(id+"F0.wireOp",EDGE,"E9.MirrorCS"),sQuery(id+"F0.wireOp",EDGE,"E10.MirrorCS"),sQuery(id+"F0.wireOp",EDGE,"E11.MirrorCS"),sQuery(id+"F0.wireOp",EDGE,"E12")])]}),"instanceName":"36"});
            var Q41;
            Q41=makeQuery(id+"F2.opPattern","COPY",BODY,{"derivedFrom":makeQuery(id+"F1.opExtrude","SWEPT_BODY",BODY,{"disambiguationData":[OSD([sQuery(id+"F0.wireOp",EDGE,"E1"),sQuery(id+"F0.wireOp",EDGE,"E3"),sQuery(id+"F0.wireOp",EDGE,"E5"),sQuery(id+"F0.wireOp",EDGE,"E6"),sQuery(id+"F0.wireOp",EDGE,"E7.filletArc"),sQuery(id+"F0.wireOp",EDGE,"E8.MirrorCS"),sQuery(id+"F0.wireOp",EDGE,"E9.MirrorCS"),sQuery(id+"F0.wireOp",EDGE,"E10.MirrorCS"),sQuery(id+"F0.wireOp",EDGE,"E11.MirrorCS"),sQuery(id+"F0.wireOp",EDGE,"E12")])]}),"instanceName":"37"});
            var Q42;
            Q42=makeQuery(id+"F2.opPattern","COPY",BODY,{"derivedFrom":makeQuery(id+"F1.opExtrude","SWEPT_BODY",BODY,{"disambiguationData":[OSD([sQuery(id+"F0.wireOp",EDGE,"E1"),sQuery(id+"F0.wireOp",EDGE,"E3"),sQuery(id+"F0.wireOp",EDGE,"E5"),sQuery(id+"F0.wireOp",EDGE,"E6"),sQuery(id+"F0.wireOp",EDGE,"E7.filletArc"),sQuery(id+"F0.wireOp",EDGE,"E8.MirrorCS"),sQuery(id+"F0.wireOp",EDGE,"E9.MirrorCS"),sQuery(id+"F0.wireOp",EDGE,"E10.MirrorCS"),sQuery(id+"F0.wireOp",EDGE,"E11.MirrorCS"),sQuery(id+"F0.wireOp",EDGE,"E12")])]}),"instanceName":"38"});
            var Q43;
            Q43=makeQuery(id+"F2.opPattern","COPY",BODY,{"derivedFrom":makeQuery(id+"F1.opExtrude","SWEPT_BODY",BODY,{"disambiguationData":[OSD([sQuery(id+"F0.wireOp",EDGE,"E1"),sQuery(id+"F0.wireOp",EDGE,"E3"),sQuery(id+"F0.wireOp",EDGE,"E5"),sQuery(id+"F0.wireOp",EDGE,"E6"),sQuery(id+"F0.wireOp",EDGE,"E7.filletArc"),sQuery(id+"F0.wireOp",EDGE,"E8.MirrorCS"),sQuery(id+"F0.wireOp",EDGE,"E9.MirrorCS"),sQuery(id+"F0.wireOp",EDGE,"E10.MirrorCS"),sQuery(id+"F0.wireOp",EDGE,"E11.MirrorCS"),sQuery(id+"F0.wireOp",EDGE,"E12")])]}),"instanceName":"39"});
            var Q44;
            Q44=makeQuery(id+"F2.opPattern","COPY",BODY,{"derivedFrom":makeQuery(id+"F1.opExtrude","SWEPT_BODY",BODY,{"disambiguationData":[OSD([sQuery(id+"F0.wireOp",EDGE,"E1"),sQuery(id+"F0.wireOp",EDGE,"E3"),sQuery(id+"F0.wireOp",EDGE,"E5"),sQuery(id+"F0.wireOp",EDGE,"E6"),sQuery(id+"F0.wireOp",EDGE,"E7.filletArc"),sQuery(id+"F0.wireOp",EDGE,"E8.MirrorCS"),sQuery(id+"F0.wireOp",EDGE,"E9.MirrorCS"),sQuery(id+"F0.wireOp",EDGE,"E10.MirrorCS"),sQuery(id+"F0.wireOp",EDGE,"E11.MirrorCS"),sQuery(id+"F0.wireOp",EDGE,"E12")])]}),"instanceName":"40"});
            var Q45;
            Q45=makeQuery(id+"F2.opPattern","COPY",BODY,{"derivedFrom":makeQuery(id+"F1.opExtrude","SWEPT_BODY",BODY,{"disambiguationData":[OSD([sQuery(id+"F0.wireOp",EDGE,"E1"),sQuery(id+"F0.wireOp",EDGE,"E3"),sQuery(id+"F0.wireOp",EDGE,"E5"),sQuery(id+"F0.wireOp",EDGE,"E6"),sQuery(id+"F0.wireOp",EDGE,"E7.filletArc"),sQuery(id+"F0.wireOp",EDGE,"E8.MirrorCS"),sQuery(id+"F0.wireOp",EDGE,"E9.MirrorCS"),sQuery(id+"F0.wireOp",EDGE,"E10.MirrorCS"),sQuery(id+"F0.wireOp",EDGE,"E11.MirrorCS"),sQuery(id+"F0.wireOp",EDGE,"E12")])]}),"instanceName":"41"});
            var Q46;
            Q46=makeQuery(id+"F2.opPattern","COPY",BODY,{"derivedFrom":makeQuery(id+"F1.opExtrude","SWEPT_BODY",BODY,{"disambiguationData":[OSD([sQuery(id+"F0.wireOp",EDGE,"E1"),sQuery(id+"F0.wireOp",EDGE,"E3"),sQuery(id+"F0.wireOp",EDGE,"E5"),sQuery(id+"F0.wireOp",EDGE,"E6"),sQuery(id+"F0.wireOp",EDGE,"E7.filletArc"),sQuery(id+"F0.wireOp",EDGE,"E8.MirrorCS"),sQuery(id+"F0.wireOp",EDGE,"E9.MirrorCS"),sQuery(id+"F0.wireOp",EDGE,"E10.MirrorCS"),sQuery(id+"F0.wireOp",EDGE,"E11.MirrorCS"),sQuery(id+"F0.wireOp",EDGE,"E12")])]}),"instanceName":"42"});
            var Q47;
            Q47=makeQuery(id+"F2.opPattern","COPY",BODY,{"derivedFrom":makeQuery(id+"F1.opExtrude","SWEPT_BODY",BODY,{"disambiguationData":[OSD([sQuery(id+"F0.wireOp",EDGE,"E1"),sQuery(id+"F0.wireOp",EDGE,"E3"),sQuery(id+"F0.wireOp",EDGE,"E5"),sQuery(id+"F0.wireOp",EDGE,"E6"),sQuery(id+"F0.wireOp",EDGE,"E7.filletArc"),sQuery(id+"F0.wireOp",EDGE,"E8.MirrorCS"),sQuery(id+"F0.wireOp",EDGE,"E9.MirrorCS"),sQuery(id+"F0.wireOp",EDGE,"E10.MirrorCS"),sQuery(id+"F0.wireOp",EDGE,"E11.MirrorCS"),sQuery(id+"F0.wireOp",EDGE,"E12")])]}),"instanceName":"43"});
            var Q48;
            Q48=makeQuery(id+"F2.opPattern","COPY",BODY,{"derivedFrom":makeQuery(id+"F1.opExtrude","SWEPT_BODY",BODY,{"disambiguationData":[OSD([sQuery(id+"F0.wireOp",EDGE,"E1"),sQuery(id+"F0.wireOp",EDGE,"E3"),sQuery(id+"F0.wireOp",EDGE,"E5"),sQuery(id+"F0.wireOp",EDGE,"E6"),sQuery(id+"F0.wireOp",EDGE,"E7.filletArc"),sQuery(id+"F0.wireOp",EDGE,"E8.MirrorCS"),sQuery(id+"F0.wireOp",EDGE,"E9.MirrorCS"),sQuery(id+"F0.wireOp",EDGE,"E10.MirrorCS"),sQuery(id+"F0.wireOp",EDGE,"E11.MirrorCS"),sQuery(id+"F0.wireOp",EDGE,"E12")])]}),"instanceName":"44"});
            var Q49;
            Q49=makeQuery(id+"F2.opPattern","COPY",BODY,{"derivedFrom":makeQuery(id+"F1.opExtrude","SWEPT_BODY",BODY,{"disambiguationData":[OSD([sQuery(id+"F0.wireOp",EDGE,"E1"),sQuery(id+"F0.wireOp",EDGE,"E3"),sQuery(id+"F0.wireOp",EDGE,"E5"),sQuery(id+"F0.wireOp",EDGE,"E6"),sQuery(id+"F0.wireOp",EDGE,"E7.filletArc"),sQuery(id+"F0.wireOp",EDGE,"E8.MirrorCS"),sQuery(id+"F0.wireOp",EDGE,"E9.MirrorCS"),sQuery(id+"F0.wireOp",EDGE,"E10.MirrorCS"),sQuery(id+"F0.wireOp",EDGE,"E11.MirrorCS"),sQuery(id+"F0.wireOp",EDGE,"E12")])]}),"instanceName":"45"});
            var Q50;
            Q50=makeQuery(id+"F2.opPattern","COPY",BODY,{"derivedFrom":makeQuery(id+"F1.opExtrude","SWEPT_BODY",BODY,{"disambiguationData":[OSD([sQuery(id+"F0.wireOp",EDGE,"E1"),sQuery(id+"F0.wireOp",EDGE,"E3"),sQuery(id+"F0.wireOp",EDGE,"E5"),sQuery(id+"F0.wireOp",EDGE,"E6"),sQuery(id+"F0.wireOp",EDGE,"E7.filletArc"),sQuery(id+"F0.wireOp",EDGE,"E8.MirrorCS"),sQuery(id+"F0.wireOp",EDGE,"E9.MirrorCS"),sQuery(id+"F0.wireOp",EDGE,"E10.MirrorCS"),sQuery(id+"F0.wireOp",EDGE,"E11.MirrorCS"),sQuery(id+"F0.wireOp",EDGE,"E12")])]}),"instanceName":"46"});
            var Q51;
            Q51=makeQuery(id+"F2.opPattern","COPY",BODY,{"derivedFrom":makeQuery(id+"F1.opExtrude","SWEPT_BODY",BODY,{"disambiguationData":[OSD([sQuery(id+"F0.wireOp",EDGE,"E1"),sQuery(id+"F0.wireOp",EDGE,"E3"),sQuery(id+"F0.wireOp",EDGE,"E5"),sQuery(id+"F0.wireOp",EDGE,"E6"),sQuery(id+"F0.wireOp",EDGE,"E7.filletArc"),sQuery(id+"F0.wireOp",EDGE,"E8.MirrorCS"),sQuery(id+"F0.wireOp",EDGE,"E9.MirrorCS"),sQuery(id+"F0.wireOp",EDGE,"E10.MirrorCS"),sQuery(id+"F0.wireOp",EDGE,"E11.MirrorCS"),sQuery(id+"F0.wireOp",EDGE,"E12")])]}),"instanceName":"47"});
            var Q52;
            Q52=makeQuery(id+"F2.opPattern","COPY",BODY,{"derivedFrom":makeQuery(id+"F1.opExtrude","SWEPT_BODY",BODY,{"disambiguationData":[OSD([sQuery(id+"F0.wireOp",EDGE,"E1"),sQuery(id+"F0.wireOp",EDGE,"E3"),sQuery(id+"F0.wireOp",EDGE,"E5"),sQuery(id+"F0.wireOp",EDGE,"E6"),sQuery(id+"F0.wireOp",EDGE,"E7.filletArc"),sQuery(id+"F0.wireOp",EDGE,"E8.MirrorCS"),sQuery(id+"F0.wireOp",EDGE,"E9.MirrorCS"),sQuery(id+"F0.wireOp",EDGE,"E10.MirrorCS"),sQuery(id+"F0.wireOp",EDGE,"E11.MirrorCS"),sQuery(id+"F0.wireOp",EDGE,"E12")])]}),"instanceName":"48"});
            var Q53;
            Q53=makeQuery(id+"F2.opPattern","COPY",BODY,{"derivedFrom":makeQuery(id+"F1.opExtrude","SWEPT_BODY",BODY,{"disambiguationData":[OSD([sQuery(id+"F0.wireOp",EDGE,"E1"),sQuery(id+"F0.wireOp",EDGE,"E3"),sQuery(id+"F0.wireOp",EDGE,"E5"),sQuery(id+"F0.wireOp",EDGE,"E6"),sQuery(id+"F0.wireOp",EDGE,"E7.filletArc"),sQuery(id+"F0.wireOp",EDGE,"E8.MirrorCS"),sQuery(id+"F0.wireOp",EDGE,"E9.MirrorCS"),sQuery(id+"F0.wireOp",EDGE,"E10.MirrorCS"),sQuery(id+"F0.wireOp",EDGE,"E11.MirrorCS"),sQuery(id+"F0.wireOp",EDGE,"E12")])]}),"instanceName":"49"});
            var Q54;
            Q54=makeQuery(id+"F2.opPattern","COPY",BODY,{"derivedFrom":makeQuery(id+"F1.opExtrude","SWEPT_BODY",BODY,{"disambiguationData":[OSD([sQuery(id+"F0.wireOp",EDGE,"E1"),sQuery(id+"F0.wireOp",EDGE,"E3"),sQuery(id+"F0.wireOp",EDGE,"E5"),sQuery(id+"F0.wireOp",EDGE,"E6"),sQuery(id+"F0.wireOp",EDGE,"E7.filletArc"),sQuery(id+"F0.wireOp",EDGE,"E8.MirrorCS"),sQuery(id+"F0.wireOp",EDGE,"E9.MirrorCS"),sQuery(id+"F0.wireOp",EDGE,"E10.MirrorCS"),sQuery(id+"F0.wireOp",EDGE,"E11.MirrorCS"),sQuery(id+"F0.wireOp",EDGE,"E12")])]}),"instanceName":"50"});
            var Q55;
            Q55=makeQuery(id+"F2.opPattern","COPY",BODY,{"derivedFrom":makeQuery(id+"F1.opExtrude","SWEPT_BODY",BODY,{"disambiguationData":[OSD([sQuery(id+"F0.wireOp",EDGE,"E1"),sQuery(id+"F0.wireOp",EDGE,"E3"),sQuery(id+"F0.wireOp",EDGE,"E5"),sQuery(id+"F0.wireOp",EDGE,"E6"),sQuery(id+"F0.wireOp",EDGE,"E7.filletArc"),sQuery(id+"F0.wireOp",EDGE,"E8.MirrorCS"),sQuery(id+"F0.wireOp",EDGE,"E9.MirrorCS"),sQuery(id+"F0.wireOp",EDGE,"E10.MirrorCS"),sQuery(id+"F0.wireOp",EDGE,"E11.MirrorCS"),sQuery(id+"F0.wireOp",EDGE,"E12")])]}),"instanceName":"51"});
            var Q56;
            Q56=makeQuery(id+"F2.opPattern","COPY",BODY,{"derivedFrom":makeQuery(id+"F1.opExtrude","SWEPT_BODY",BODY,{"disambiguationData":[OSD([sQuery(id+"F0.wireOp",EDGE,"E1"),sQuery(id+"F0.wireOp",EDGE,"E3"),sQuery(id+"F0.wireOp",EDGE,"E5"),sQuery(id+"F0.wireOp",EDGE,"E6"),sQuery(id+"F0.wireOp",EDGE,"E7.filletArc"),sQuery(id+"F0.wireOp",EDGE,"E8.MirrorCS"),sQuery(id+"F0.wireOp",EDGE,"E9.MirrorCS"),sQuery(id+"F0.wireOp",EDGE,"E10.MirrorCS"),sQuery(id+"F0.wireOp",EDGE,"E11.MirrorCS"),sQuery(id+"F0.wireOp",EDGE,"E12")])]}),"instanceName":"52"});
            var Q57;
            Q57=makeQuery(id+"F2.opPattern","COPY",BODY,{"derivedFrom":makeQuery(id+"F1.opExtrude","SWEPT_BODY",BODY,{"disambiguationData":[OSD([sQuery(id+"F0.wireOp",EDGE,"E1"),sQuery(id+"F0.wireOp",EDGE,"E3"),sQuery(id+"F0.wireOp",EDGE,"E5"),sQuery(id+"F0.wireOp",EDGE,"E6"),sQuery(id+"F0.wireOp",EDGE,"E7.filletArc"),sQuery(id+"F0.wireOp",EDGE,"E8.MirrorCS"),sQuery(id+"F0.wireOp",EDGE,"E9.MirrorCS"),sQuery(id+"F0.wireOp",EDGE,"E10.MirrorCS"),sQuery(id+"F0.wireOp",EDGE,"E11.MirrorCS"),sQuery(id+"F0.wireOp",EDGE,"E12")])]}),"instanceName":"53"});
            var Q58;
            Q58=makeQuery(id+"F2.opPattern","COPY",BODY,{"derivedFrom":makeQuery(id+"F1.opExtrude","SWEPT_BODY",BODY,{"disambiguationData":[OSD([sQuery(id+"F0.wireOp",EDGE,"E1"),sQuery(id+"F0.wireOp",EDGE,"E3"),sQuery(id+"F0.wireOp",EDGE,"E5"),sQuery(id+"F0.wireOp",EDGE,"E6"),sQuery(id+"F0.wireOp",EDGE,"E7.filletArc"),sQuery(id+"F0.wireOp",EDGE,"E8.MirrorCS"),sQuery(id+"F0.wireOp",EDGE,"E9.MirrorCS"),sQuery(id+"F0.wireOp",EDGE,"E10.MirrorCS"),sQuery(id+"F0.wireOp",EDGE,"E11.MirrorCS"),sQuery(id+"F0.wireOp",EDGE,"E12")])]}),"instanceName":"54"});
            var Q59;
            Q59=makeQuery(id+"F2.opPattern","COPY",BODY,{"derivedFrom":makeQuery(id+"F1.opExtrude","SWEPT_BODY",BODY,{"disambiguationData":[OSD([sQuery(id+"F0.wireOp",EDGE,"E1"),sQuery(id+"F0.wireOp",EDGE,"E3"),sQuery(id+"F0.wireOp",EDGE,"E5"),sQuery(id+"F0.wireOp",EDGE,"E6"),sQuery(id+"F0.wireOp",EDGE,"E7.filletArc"),sQuery(id+"F0.wireOp",EDGE,"E8.MirrorCS"),sQuery(id+"F0.wireOp",EDGE,"E9.MirrorCS"),sQuery(id+"F0.wireOp",EDGE,"E10.MirrorCS"),sQuery(id+"F0.wireOp",EDGE,"E11.MirrorCS"),sQuery(id+"F0.wireOp",EDGE,"E12")])]}),"instanceName":"55"});
            hole(context, id + "F4", {"style" : HoleStyle.SIMPLE, "endStyle" : HoleEndStyle.THROUGH, "holeDiameter" : 6.35 * mm, "locations" : qUnion([Q0, Q1, Q2, Q3]), "scope" : qUnion([Q4, Q5, Q6, Q7, Q8, Q9, Q10, Q11, Q12, Q13, Q14, Q15, Q16, Q17, Q18, Q19, Q20, Q21, Q22, Q23, Q24, Q25, Q26, Q27, Q28, Q29, Q30, Q31, Q32, Q33, Q34, Q35, Q36, Q37, Q38, Q39, Q40, Q41, Q42, Q43, Q44, Q45, Q46, Q47, Q48, Q49, Q50, Q51, Q52, Q53, Q54, Q55, Q56, Q57, Q58, Q59]), "isTappedThrough" : true});
        }
    });
